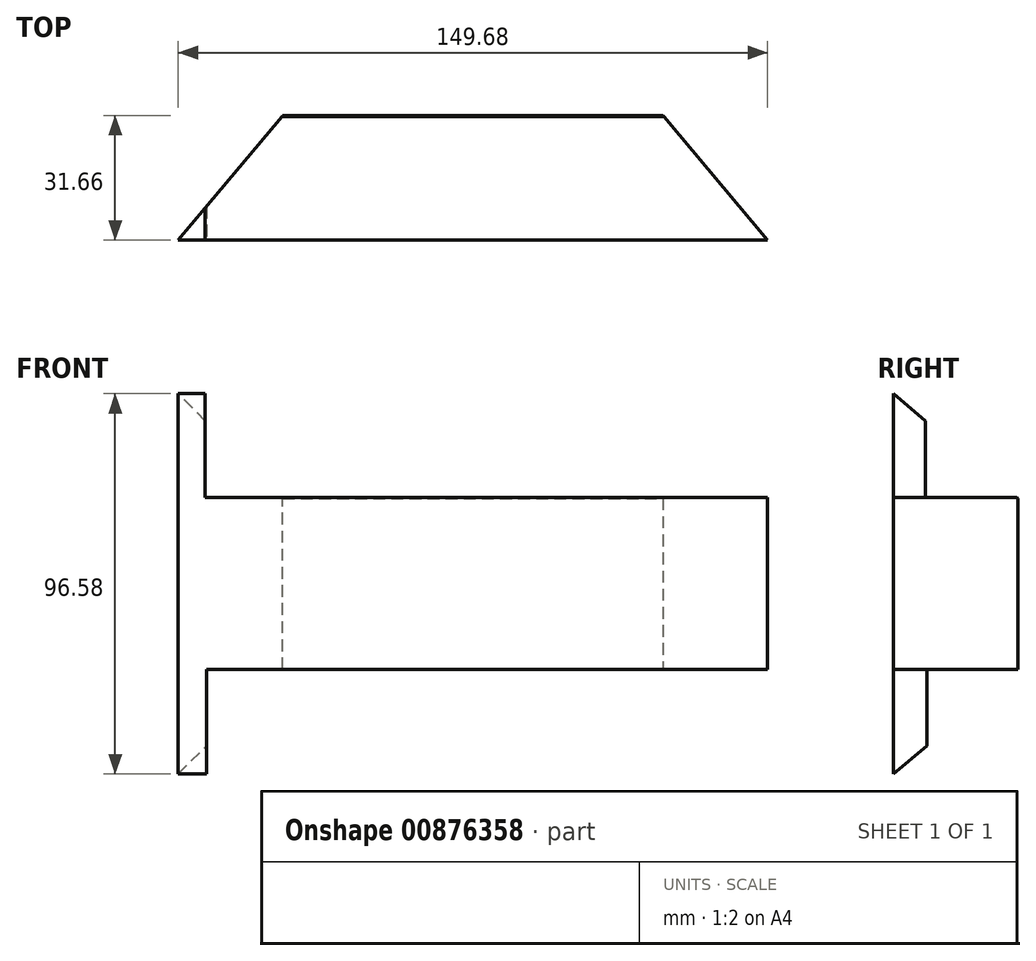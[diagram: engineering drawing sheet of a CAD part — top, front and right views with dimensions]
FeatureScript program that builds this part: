
annotation { "Feature Type Name" : "Feature", "Feature Type Description" : "" }
export const myFeature = defineFeature(function(context is Context, id is Id, definition is map)
    precondition{}
    {
        {
            var Q0;
            Q0=qCreatedBy(makeId("Front.planeOp"),FACE);
            var sketch = newSketch(context, id + "F0", { "sketchPlane" : qUnion([Q0])});
            skLineSegment(sketch, "E0.bottom", {"start": v(48.28, -21.73) * mm, "end": v(-48.28, -21.73) * mm});
            skLineSegment(sketch, "E0.top", {"start": v(48.28, 21.73) * mm, "end": v(-48.28, 21.73) * mm});
            skLineSegment(sketch, "E0.left", {"start": v(48.28, -21.73) * mm, "end": v(48.28, 21.73) * mm});
            skLineSegment(sketch, "E0.right", {"start": v(-48.28, -21.73) * mm, "end": v(-48.28, 21.73) * mm});
            skPoint(sketch, "E0.middle", {"position": v(0, 0) * mm});
            skSolve(sketch);
        }
        {
            var Q0;
            Q0=makeQuery(id+"F0.imprint","IMPRINT",FACE,{"disambiguationData":[TD([[makeQuery(id+"F0.imprint","IMPRINT",EDGE,{"derivedFrom":sQuery(id+"F0.wireOp",EDGE,"E0.bottom")}),-1.0]])]});
            extrude(context, id + "F1", {"entities" : qUnion([Q0]), "depth" : 31.66 * mm, "offsetDistance" : 25.4 * mm, "hasDraft" : true, "draftAngle" : 40 * degree});
        }
        {
            var Q0;
            Q0=qCreatedBy(makeId("Front.planeOp"),FACE);
            var sketch = newSketch(context, id + "F2", { "sketchPlane" : qUnion([Q0])});
            skLineSegment(sketch, "E1.bottom", {"start": v(-67.96, 21.95) * mm, "end": v(94.92, 21.95) * mm});
            skLineSegment(sketch, "E1.top", {"start": v(-67.96, 53.8) * mm, "end": v(94.92, 53.8) * mm});
            skLineSegment(sketch, "E1.left", {"start": v(-67.96, 21.95) * mm, "end": v(-67.96, 53.8) * mm});
            skLineSegment(sketch, "E1.right", {"start": v(94.92, 21.95) * mm, "end": v(94.92, 53.8) * mm});
            skLineSegment(sketch, "E2.bottom", {"start": v(-67.67, -21.72) * mm, "end": v(99.35, -21.72) * mm});
            skLineSegment(sketch, "E2.top", {"start": v(-67.67, -60.08) * mm, "end": v(99.35, -60.08) * mm});
            skLineSegment(sketch, "E2.left", {"start": v(-67.67, -21.72) * mm, "end": v(-67.67, -60.08) * mm});
            skLineSegment(sketch, "E2.right", {"start": v(99.35, -21.72) * mm, "end": v(99.35, -60.08) * mm});
            skSolve(sketch);
        }
        {
            var Q0;
            Q0=makeQuery(id+"F2.imprint","IMPRINT",FACE,{"disambiguationData":[TD([[makeQuery(id+"F2.imprint","IMPRINT",EDGE,{"derivedFrom":sQuery(id+"F2.wireOp",EDGE,"E2.bottom")}),-1.0]])]});
            var Q1;
            Q1=makeQuery(id+"F2.imprint","IMPRINT",FACE,{"disambiguationData":[TD([[makeQuery(id+"F2.imprint","IMPRINT",EDGE,{"derivedFrom":sQuery(id+"F2.wireOp",EDGE,"E1.bottom")}),1.0]])]});
            extrude(context, id + "F3", {"entities" : qUnion([Q0, Q1]), "operationType" : NewBodyOperationType.REMOVE, "depth" : 79.45 * mm, "offsetDistance" : 25.4 * mm});
        }
        {
            var Q0;
            Q0=qCreatedBy(makeId("Front.planeOp"),FACE);
            var sketch = newSketch(context, id + "F4", { "sketchPlane" : qUnion([Q0])});
            skLineSegment(sketch, "E3.bottom", {"start": v(-76.97, 22.25) * mm, "end": v(-55.85, 22.25) * mm});
            skLineSegment(sketch, "E3.top", {"start": v(-76.97, 55.14) * mm, "end": v(-55.85, 55.14) * mm});
            skLineSegment(sketch, "E3.left", {"start": v(-76.97, 22.25) * mm, "end": v(-76.97, 55.14) * mm});
            skLineSegment(sketch, "E3.right", {"start": v(-55.85, 22.25) * mm, "end": v(-55.85, 55.14) * mm});
            skLineSegment(sketch, "E4.bottom", {"start": v(-75.83, -21.34) * mm, "end": v(-39.02, -21.34) * mm});
            skLineSegment(sketch, "E4.top", {"start": v(-75.83, -48.13) * mm, "end": v(-39.02, -48.13) * mm});
            skLineSegment(sketch, "E4.left", {"start": v(-75.83, -21.34) * mm, "end": v(-75.83, -48.13) * mm});
            skLineSegment(sketch, "E4.right", {"start": v(-39.02, -21.34) * mm, "end": v(-39.02, -48.13) * mm});
            skSolve(sketch);
        }
        {
            var Q0;
            Q0=makeQuery(id+"F4.imprint","IMPRINT",FACE,{"disambiguationData":[TD([[makeQuery(id+"F4.imprint","IMPRINT",EDGE,{"derivedFrom":sQuery(id+"F4.wireOp",EDGE,"E3.bottom")}),1.0]])]});
            extrude(context, id + "F5", {"entities" : qUnion([Q0]), "operationType" : NewBodyOperationType.REMOVE, "depth" : 14.5 * mm, "offsetDistance" : 25.4 * mm});
        }
    });
